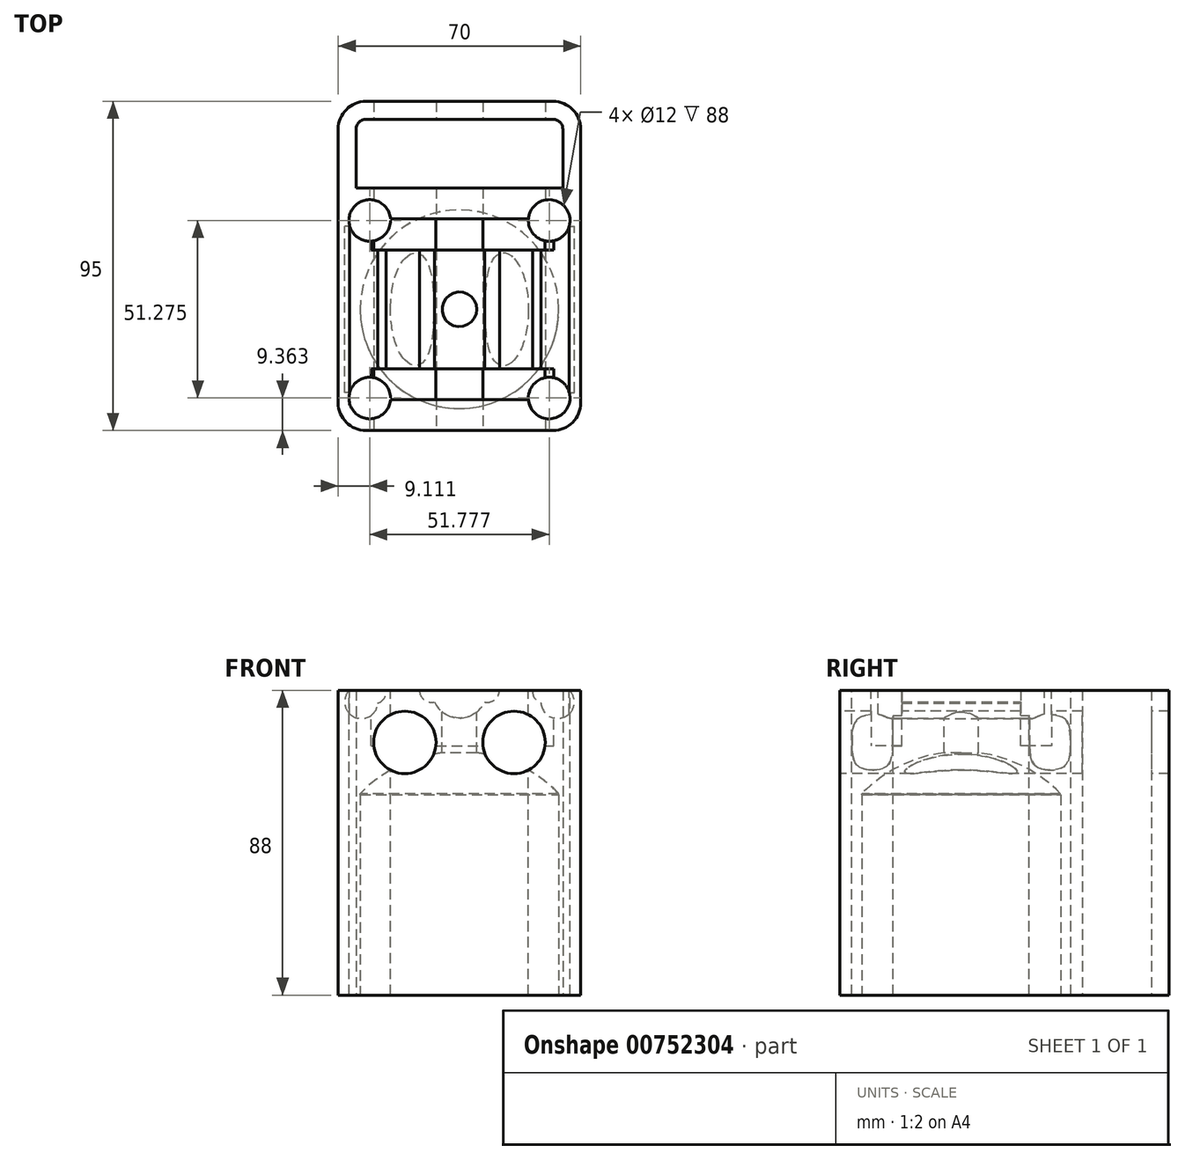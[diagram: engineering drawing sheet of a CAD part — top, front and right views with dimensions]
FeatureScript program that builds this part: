
annotation { "Feature Type Name" : "Feature", "Feature Type Description" : "" }
export const myFeature = defineFeature(function(context is Context, id is Id, definition is map)
    precondition{}
    {
        {
            var Q0;
            Q0=qCreatedBy(makeId("Top.planeOp"),FACE);
            var sketch = newSketch(context, id + "F0", { "sketchPlane" : qUnion([Q0])});
            skLineSegment(sketch, "E0.bottom", {"start": v(35, 35) * mm, "end": v(-35, 35) * mm});
            skLineSegment(sketch, "E0.top", {"start": v(27, -35) * mm, "end": v(-27, -35) * mm});
            skLineSegment(sketch, "E0.left", {"start": v(35, 35) * mm, "end": v(35, -27) * mm});
            skLineSegment(sketch, "E0.right", {"start": v(-35, 35) * mm, "end": v(-35, -27) * mm});
            skPoint(sketch, "E0.middle", {"position": v(0, 0) * mm});
            skPoint(sketch, "E1.visualSharp", {"position": v(-35, 35) * mm});
            skLineSegment(sketch, "E1.filletArc", {"start": v(-35, 35) * mm, "end": v(-35, 35) * mm});
            skPoint(sketch, "E2.visualSharp", {"position": v(35, 35) * mm});
            skLineSegment(sketch, "E2.filletArc", {"start": v(35, 35) * mm, "end": v(35, 35) * mm});
            skPoint(sketch, "E3.visualSharp", {"position": v(-35, -35) * mm});
            skArc(sketch, "E3.filletArc", {"start": v(-35, -27) * mm, "mid": v(-32.66, -32.66) * mm, "end": v(-27, -35) * mm});
            skPoint(sketch, "E4.visualSharp", {"position": v(35, -35) * mm});
            skArc(sketch, "E4.filletArc", {"start": v(27, -35) * mm, "mid": v(32.66, -32.66) * mm, "end": v(35, -27) * mm});
            skLineSegment(sketch, "E5.bottom", {"start": v(-35, 35) * mm, "end": v(35, 35) * mm});
            skLineSegment(sketch, "E5.top", {"start": v(-27, 60) * mm, "end": v(27, 60) * mm});
            skLineSegment(sketch, "E5.left", {"start": v(-35, 35) * mm, "end": v(-35, 52) * mm});
            skLineSegment(sketch, "E5.right", {"start": v(35, 35) * mm, "end": v(35, 52) * mm});
            skPoint(sketch, "E6.visualSharp", {"position": v(-35, 60) * mm});
            skArc(sketch, "E6.filletArc", {"start": v(-27, 60) * mm, "mid": v(-32.66, 57.66) * mm, "end": v(-35, 52) * mm});
            skPoint(sketch, "E7.visualSharp", {"position": v(35, 60) * mm});
            skArc(sketch, "E7.filletArc", {"start": v(35, 52) * mm, "mid": v(32.66, 57.66) * mm, "end": v(27, 60) * mm});
            skLineSegment(sketch, "E8.0", {"start": v(-27, 55) * mm, "end": v(27, 55) * mm});
            skArc(sketch, "E9.0", {"start": v(-27, 55) * mm, "mid": v(-29.12, 54.12) * mm, "end": v(-30, 52) * mm});
            skLineSegment(sketch, "E10.0", {"start": v(29.83, 35) * mm, "end": v(29.83, 52) * mm});
            skLineSegment(sketch, "E10.1", {"start": v(-29.83, 35) * mm, "end": v(-29.83, 52) * mm});
            skArc(sketch, "E10.2", {"start": v(-27, 54.83) * mm, "mid": v(-29, 54) * mm, "end": v(-29.83, 52) * mm});
            skLineSegment(sketch, "E10.3", {"start": v(-27, 54.83) * mm, "end": v(27, 54.83) * mm});
            skArc(sketch, "E10.4", {"start": v(29.83, 52) * mm, "mid": v(29, 54) * mm, "end": v(27, 54.83) * mm});
            skSolve(sketch);
        }
        {
            var Q0;
            Q0=makeQuery(id+"F0.imprint","IMPRINT",FACE,{"disambiguationData":[TD([[makeQuery(id+"F0.imprint","IMPRINT",EDGE,{"derivedFrom":sQuery(id+"F0.wireOp",EDGE,"E0.bottom")}),1.0]])]});
            var Q1;
            Q1=makeQuery(id+"F0.imprint","IMPRINT",FACE,{"disambiguationData":[TD([[makeQuery(id+"F0.imprint","IMPRINT",EDGE,{"derivedFrom":sQuery(id+"F0.wireOp",EDGE,"E0.top")}),-1.0]])]});
            var Q2;
            Q2=makeQuery(id+"F0.imprint","IMPRINT",FACE,{"disambiguationData":[TD([[makeQuery(id+"F0.imprint","IMPRINT",EDGE,{"derivedFrom":sQuery(id+"F0.wireOp",EDGE,"E5.top")}),-1.0]])]});
            extrude(context, id + "F1", {"entities" : qUnion([Q0, Q1, Q2]), "depth" : 30 * mm, "offsetDistance" : 25 * mm, "hasSecondDirection" : true, "secondDirectionOppositeDirection" : true, "secondDirectionDepth" : 58 * mm});
        }
        {
            var Q0;
            Q0 = qSketchRegion(id + "F0", true);
            extrude(context, id + "F2", {"entities" : qUnion([Q0]), "operationType" : NewBodyOperationType.ADD, "oppositeDirection" : true, "depth" : 2 * mm, "offsetDistance" : 25 * mm});
        }
        {
            var Q0;
            Q0=makeQuery(id+"F1.opExtrude","CAP_FACE",FACE,{"disambiguationData":[OSD([sQuery(id+"F0.wireOp",EDGE,"E0.bottom"),sQuery(id+"F0.wireOp",EDGE,"E0.top"),sQuery(id+"F0.wireOp",EDGE,"E0.left"),sQuery(id+"F0.wireOp",EDGE,"E0.right")])],"isStart":true});
            var sketch = newSketch(context, id + "F3", { "sketchPlane" : qUnion([Q0])});
            skCircle(sketch, "E11", {"center": v(0, 0) * mm, "radius": 28.66 * mm});
            skSolve(sketch);
        }
        {
            var Q0;
            Q0=makeQuery(id+"F1.opExtrude","SWEPT_FACE",FACE,{"disambiguationData":[OSD([sQuery(id+"F0.wireOp",EDGE,"E0.top")])]});
            var sketch = newSketch(context, id + "F4", { "sketchPlane" : qUnion([Q0])});
            skCircle(sketch, "E12", {"center": v(-15.75, 14.97) * mm, "radius": 9 * mm});
            skCircle(sketch, "E13.MirrorC", {"center": v(15.75, 14.97) * mm, "radius": 9 * mm});
            skSolve(sketch);
        }
        {
            var Q0;
            Q0 = qSketchRegion(id + "F4", true);
            extrude(context, id + "F5", {"entities" : qUnion([Q0]), "operationType" : NewBodyOperationType.REMOVE, "endBound" : BoundingType.THROUGH_ALL, "oppositeDirection" : true, "depth" : 25 * mm, "offsetDistance" : 25 * mm});
        }
        {
            var Q0;
            Q0=makeQuery(id+"F1.opExtrude","CAP_FACE",FACE,{"disambiguationData":[OSD([sQuery(id+"F0.wireOp",EDGE,"E0.bottom"),sQuery(id+"F0.wireOp",EDGE,"E0.top"),sQuery(id+"F0.wireOp",EDGE,"E0.left"),sQuery(id+"F0.wireOp",EDGE,"E0.right")])],"isStart":false});
            var sketch = newSketch(context, id + "F6", { "sketchPlane" : qUnion([Q0])});
            skCircle(sketch, "E14", {"center": v(0, 0) * mm, "radius": 5 * mm});
            skSolve(sketch);
        }
        {
            var Q0;
            Q0 = qSketchRegion(id + "F6", true);
            extrude(context, id + "F7", {"entities" : qUnion([Q0]), "operationType" : NewBodyOperationType.REMOVE, "endBound" : BoundingType.THROUGH_ALL, "oppositeDirection" : true, "depth" : 25 * mm, "offsetDistance" : 25 * mm});
        }
        {
            var Q0;
            Q0=qCreatedBy(makeId("Front.planeOp"),FACE);
            var sketch = newSketch(context, id + "F8", { "sketchPlane" : qUnion([Q0])});
            skLineSegment(sketch, "E15", {"start": v(0, 30.69) * mm, "end": v(0, 0) * mm});
            skLineSegment(sketch, "E16.bottom", {"start": v(35.16, 0) * mm, "end": v(0, 0) * mm});
            skLineSegment(sketch, "E16.top", {"start": v(35.16, 30.69) * mm, "end": v(0, 30.69) * mm});
            skLineSegment(sketch, "E16.left", {"start": v(35.16, 0) * mm, "end": v(35.16, 30.69) * mm});
            skLineSegment(sketch, "E16.right", {"start": v(0, 0) * mm, "end": v(0, 30.69) * mm});
            skSolve(sketch);
        }
        {
            var Q0;
            Q0=qCreatedBy(makeId("Front.planeOp"),FACE);
            var sketch = newSketch(context, id + "F9", { "sketchPlane" : qUnion([Q0])});
            skLineSegment(sketch, "E17.top", {"start": v(0, 0) * mm, "end": v(28.65, 0) * mm});
            skLineSegment(sketch, "E17.left", {"start": v(0, 12.27) * mm, "end": v(0, 0) * mm});
            skArc(sketch, "E18", {"start": v(0, 12.27) * mm, "mid": v(-15.55, 9.12) * mm, "end": v(-28.65, 0.18) * mm});
            skLineSegment(sketch, "E19", {"start": v(-28.65, 0.18) * mm, "end": v(0, 0) * mm});
            skLineSegment(sketch, "E20.bottom", {"start": v(-28.65, 0.18) * mm, "end": v(0, 0.18) * mm});
            skLineSegment(sketch, "E20.top", {"start": v(-28.65, -6.67) * mm, "end": v(0, -6.67) * mm});
            skLineSegment(sketch, "E20.left", {"start": v(-28.65, 0.18) * mm, "end": v(-28.65, -6.67) * mm});
            skLineSegment(sketch, "E20.right", {"start": v(0, 0.18) * mm, "end": v(0, -6.67) * mm});
            skSolve(sketch);
        }
        {
            var Q0;
            Q0 = qSketchRegion(id + "F9", true);
            var Q1;
            Q1=sQuery(id+"F8.wireOp",EDGE,"E16.right");
            revolve(context, id + "F10", {"operationType" : NewBodyOperationType.REMOVE, "surfaceOperationType" : NewSurfaceOperationType.NEW, "entities" : qUnion([Q0]), "axis" : qUnion([Q1]), "revolveType" : RevolveType.FULL, "oppositeDirection" : true});
        }
        {
            var Q0;
            Q0=makeQuery(id+"F6.imprint","IMPRINT",FACE,{"disambiguationData":[TD([[makeQuery(id+"F6.imprint","IMPRINT",EDGE,{"derivedFrom":sQuery(id+"F6.wireOp",EDGE,"E14")}),-1.0]])]});
            var sketch = newSketch(context, id + "F11", { "sketchPlane" : qUnion([Q0])});
            skSolve(sketch);
        }
        {
            var Q0;
            Q0=makeQuery(id+"F11.imprint","IMPRINT",FACE,{"disambiguationData":[TD([[makeQuery(id+"F11.imprint","IMPRINT",EDGE,{"derivedFrom":makeQuery(id+"F6.imprint","IMPRINT",EDGE,{"derivedFrom":sQuery(id+"F6.wireOp",EDGE,"E14")})}),-1.0]])]});
            var sketch = newSketch(context, id + "F12", { "sketchPlane" : qUnion([Q0])});
            skLineSegment(sketch, "E21.bottom", {"start": v(-25.54, -26.05) * mm, "end": v(27.26, -26.05) * mm});
            skLineSegment(sketch, "E21.top", {"start": v(-25.54, -17.15) * mm, "end": v(27.26, -17.15) * mm});
            skLineSegment(sketch, "E21.left", {"start": v(-25.54, -26.05) * mm, "end": v(-25.54, -17.15) * mm});
            skLineSegment(sketch, "E21.right", {"start": v(27.26, -26.05) * mm, "end": v(27.26, -17.15) * mm});
            skLineSegment(sketch, "E22.MirrorCS", {"start": v(-25.54, 17.15) * mm, "end": v(27.26, 17.15) * mm});
            skLineSegment(sketch, "E23.MirrorCS", {"start": v(-25.54, 26.05) * mm, "end": v(27.26, 26.05) * mm});
            skLineSegment(sketch, "E24.MirrorCS", {"start": v(-25.54, 26.05) * mm, "end": v(-25.54, 17.15) * mm});
            skLineSegment(sketch, "E25.MirrorCS", {"start": v(27.26, 26.05) * mm, "end": v(27.26, 17.15) * mm});
            skSolve(sketch);
        }
        {
            var Q0;
            Q0 = qSketchRegion(id + "F12", true);
            extrude(context, id + "F13", {"entities" : qUnion([Q0]), "operationType" : NewBodyOperationType.REMOVE, "oppositeDirection" : true, "depth" : 16 * mm, "offsetDistance" : 25 * mm});
        }
        {
            var Q0;
            Q0=qCreatedBy(makeId("Front.planeOp"),FACE);
            var sketch = newSketch(context, id + "F14", { "sketchPlane" : qUnion([Q0])});
            skCircle(sketch, "E26", {"center": v(0, 29.98) * mm, "radius": 8 * mm});
            skCircle(sketch, "E27", {"center": v(-8, 30.08) * mm, "radius": 3.55 * mm});
            skCircle(sketch, "E28", {"center": v(-24.66, 29.67) * mm, "radius": 3.55 * mm});
            skCircle(sketch, "E29", {"center": v(-28.33, 26.6) * mm, "radius": 4.79 * mm});
            skPoint(sketch, "E29.second.point", {"position": v(-32, 29.67) * mm});
            skPoint(sketch, "E29.third.point", {"position": v(-24.18, 24.22) * mm});
            skCircle(sketch, "E30.MirrorC", {"center": v(8, 30.08) * mm, "radius": 3.55 * mm});
            skCircle(sketch, "E31.MirrorC", {"center": v(24.66, 29.67) * mm, "radius": 3.55 * mm});
            skCircle(sketch, "E32.MirrorC", {"center": v(28.33, 26.6) * mm, "radius": 4.79 * mm});
            skSolve(sketch);
        }
        {
            var Q0;
            Q0 = qSketchRegion(id + "F14", true);
            var Q1;
            Q1=sQuery(id+"F14.wireOp",EDGE,"xoiandax-fda6-PH9P-5Wby-Ottv87CxIl39");
            var Q2;
            Q2=sQuery(id+"F14.wireOp",EDGE,"wvqkfLyV-Ojo9-pmkg-oiIu-OVvKzjCj5Hxy");
            extrude(context, id + "F15", {"entities" : qUnion([Q0]), "operationType" : NewBodyOperationType.REMOVE, "surfaceEntities" : qUnion([Q1, Q2]), "endBound" : BoundingType.SYMMETRIC, "depth" : 48 * mm, "offsetDistance" : 25 * mm});
        }
        {
            var Q0;
            Q0 = qSketchRegion(id + "F3", true);
            extrude(context, id + "F16", {"entities" : qUnion([Q0]), "operationType" : NewBodyOperationType.REMOVE, "oppositeDirection" : true, "depth" : 57.8 * mm, "offsetDistance" : 25 * mm});
        }
        {
            var Q0;
            Q0=qCreatedBy(makeId("Top.planeOp"),FACE);
            var sketch = newSketch(context, id + "F17", { "sketchPlane" : qUnion([Q0])});
            skCircle(sketch, "E33", {"center": v(-25.89, 25.64) * mm, "radius": 6 * mm});
            skPoint(sketch, "E33.first.point", {"position": v(-30.22, 21.48) * mm});
            skPoint(sketch, "E33.second.point", {"position": v(-20.59, 28.45) * mm});
            skPoint(sketch, "E33.third.point", {"position": v(-25.7, 19.64) * mm});
            skCircle(sketch, "E34.MirrorC", {"center": v(-25.89, -25.64) * mm, "radius": 6 * mm});
            skCircle(sketch, "E35.MirrorC", {"center": v(25.89, -25.64) * mm, "radius": 6 * mm});
            skCircle(sketch, "E36.MirrorC", {"center": v(25.89, 25.64) * mm, "radius": 6 * mm});
            skSolve(sketch);
        }
        {
            var Q0;
            Q0 = qSketchRegion(id + "F17", true);
            extrude(context, id + "F18", {"entities" : qUnion([Q0]), "operationType" : NewBodyOperationType.REMOVE, "endBound" : BoundingType.THROUGH_ALL, "oppositeDirection" : true, "depth" : 25 * mm, "offsetDistance" : 25 * mm, "hasSecondDirection" : true, "secondDirectionBound" : SecondDirectionBoundingType.THROUGH_ALL, "secondDirectionOppositeDirection" : false, "secondDirectionDepth" : 25 * mm});
        }
    });
